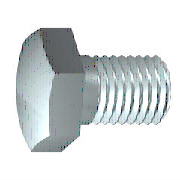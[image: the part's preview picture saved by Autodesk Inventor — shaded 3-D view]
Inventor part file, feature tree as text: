
AUTODESK INVENTOR PART (.ipt)
format: ipt  version: 2013 (Build 170138000, 138)  size: 185,856 bytes
history: native  units: mm (DEFAULTED — no unit token found)
features: sketch x2, extrude x1, chamfer x1, plane x1
ambient origin geometry x7: Origin, YZ Plane, XZ Plane, X Axis, Y Axis, Z Axis, Center Point
bodies: Solid1 (feature_tree), Body (feature_tree)
feature tree (5):
  extrude  "Head"  TaperAngle=90.0deg  [1 undecoded]
  chamfer  "Chamfer1"  [1 undecoded]
  plane  "Work Plane1"
  sketch  "Sketch1"  dims[d2=8.0mm d12=90.0deg]
  sketch  "Sketch2"  dims[d3=5.68mm d4=0.0mm d21=90.0deg d6=0.766813mm d7=0.766912mm d8=0.0mm d11=13.0mm d15=22.0mm d16=0.0mm d55=45.0deg d58=0.0mm d59=60.0mm d65=13.0mm d67=30.0deg d68=15.6mm d69=5.68mm d71=0.1mm d73=0.0mm]
note: 2 required parameter values undecoded (feature->parameter linkage not recoverable at this tier; creation-order binding heuristic only, values carry confidence <= 0.55)
